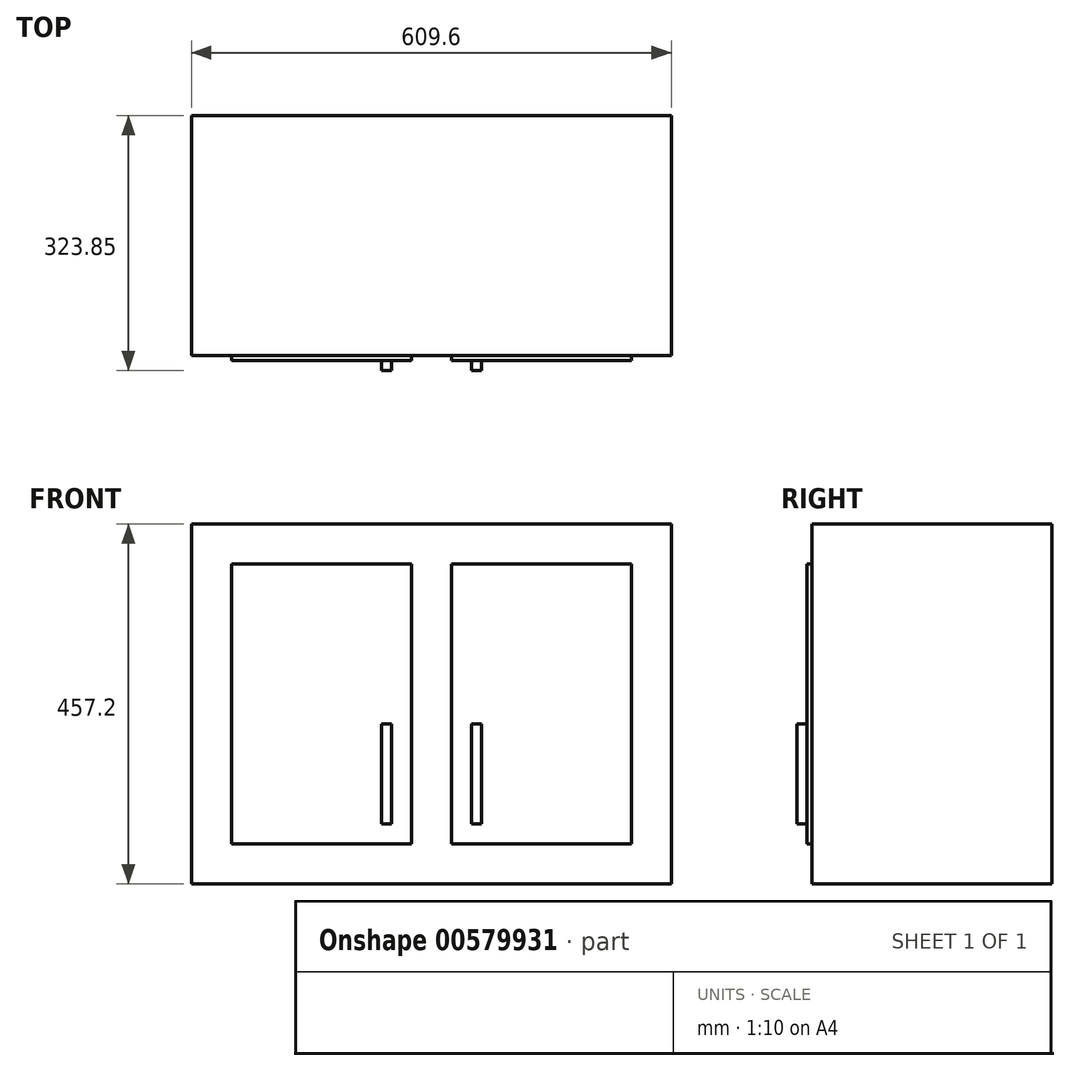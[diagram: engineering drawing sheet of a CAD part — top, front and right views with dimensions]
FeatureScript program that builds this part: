
annotation { "Feature Type Name" : "Feature", "Feature Type Description" : "" }
export const myFeature = defineFeature(function(context is Context, id is Id, definition is map)
    precondition{}
    {
        {
            var Q0;
            Q0=qCreatedBy(makeId("Front.planeOp"),FACE);
            var sketch = newSketch(context, id + "F0", { "sketchPlane" : qUnion([Q0])});
            skLineSegment(sketch, "E0.bottom", {"start": v(-332.33, 262.74) * mm, "end": v(277.27, 262.74) * mm});
            skLineSegment(sketch, "E0.top", {"start": v(-332.33, -194.46) * mm, "end": v(277.27, -194.46) * mm});
            skLineSegment(sketch, "E0.left", {"start": v(-332.33, 262.74) * mm, "end": v(-332.33, -194.46) * mm});
            skLineSegment(sketch, "E0.right", {"start": v(277.27, 262.74) * mm, "end": v(277.27, -194.46) * mm});
            skSolve(sketch);
        }
        {
            var Q0;
            Q0=makeQuery(id+"F0.imprint","IMPRINT",FACE,{"disambiguationData":[TD([[makeQuery(id+"F0.imprint","IMPRINT",EDGE,{"derivedFrom":sQuery(id+"F0.wireOp",EDGE,"E0.bottom")}),-1.0]])]});
            extrude(context, id + "F1", {"entities" : qUnion([Q0]), "depth" : 304.8 * mm, "offsetDistance" : 25.4 * mm});
        }
        {
            var Q0;
            Q0=makeQuery(id+"F1.opExtrude","CAP_FACE",FACE,{"disambiguationData":[OSD([sQuery(id+"F0.wireOp",EDGE,"E0.bottom"),sQuery(id+"F0.wireOp",EDGE,"E0.top"),sQuery(id+"F0.wireOp",EDGE,"E0.left"),sQuery(id+"F0.wireOp",EDGE,"E0.right")])],"isStart":false});
            var sketch = newSketch(context, id + "F2", { "sketchPlane" : qUnion([Q0])});
            skLineSegment(sketch, "E1.bottom", {"start": v(-281.53, 211.94) * mm, "end": v(-52.93, 211.94) * mm});
            skLineSegment(sketch, "E1.top", {"start": v(-281.53, -143.66) * mm, "end": v(-52.93, -143.66) * mm});
            skLineSegment(sketch, "E1.left", {"start": v(-281.53, 211.94) * mm, "end": v(-281.53, -143.66) * mm});
            skLineSegment(sketch, "E1.right", {"start": v(-52.93, 211.94) * mm, "end": v(-52.93, -143.66) * mm});
            skLineSegment(sketch, "E2.bottom", {"start": v(-2.13, 211.94) * mm, "end": v(226.47, 211.94) * mm});
            skLineSegment(sketch, "E2.top", {"start": v(-2.13, -143.66) * mm, "end": v(226.47, -143.66) * mm});
            skLineSegment(sketch, "E2.left", {"start": v(-2.13, 211.94) * mm, "end": v(-2.13, -143.66) * mm});
            skLineSegment(sketch, "E2.right", {"start": v(226.47, 211.94) * mm, "end": v(226.47, -143.66) * mm});
            skSolve(sketch);
        }
        {
            var Q0;
            Q0=makeQuery(id+"F2.imprint","IMPRINT",FACE,{"disambiguationData":[TD([[makeQuery(id+"F2.imprint","IMPRINT",EDGE,{"derivedFrom":sQuery(id+"F2.wireOp",EDGE,"E1.bottom")}),-1.0]])]});
            var Q1;
            Q1=makeQuery(id+"F2.imprint","IMPRINT",FACE,{"disambiguationData":[TD([[makeQuery(id+"F2.imprint","IMPRINT",EDGE,{"derivedFrom":sQuery(id+"F2.wireOp",EDGE,"E2.bottom")}),-1.0]])]});
            extrude(context, id + "F3", {"entities" : qUnion([Q0, Q1]), "operationType" : NewBodyOperationType.ADD, "depth" : 6.35 * mm, "offsetDistance" : 25.4 * mm});
        }
        {
            var Q0;
            Q0=makeQuery(id+"F3.opExtrude","CAP_FACE",FACE,{"disambiguationData":[OSD([sQuery(id+"F2.wireOp",EDGE,"E1.bottom"),sQuery(id+"F2.wireOp",EDGE,"E1.top"),sQuery(id+"F2.wireOp",EDGE,"E1.left"),sQuery(id+"F2.wireOp",EDGE,"E1.right")])],"isStart":false});
            var sketch = newSketch(context, id + "F4", { "sketchPlane" : qUnion([Q0])});
            skLineSegment(sketch, "E3.bottom", {"start": v(-91.03, 8.74) * mm, "end": v(-78.33, 8.74) * mm});
            skLineSegment(sketch, "E3.top", {"start": v(-91.03, -118.26) * mm, "end": v(-78.33, -118.26) * mm});
            skLineSegment(sketch, "E3.left", {"start": v(-91.03, 8.74) * mm, "end": v(-91.03, -118.26) * mm});
            skLineSegment(sketch, "E3.right", {"start": v(-78.33, 8.74) * mm, "end": v(-78.33, -118.26) * mm});
            skLineSegment(sketch, "E4.bottom", {"start": v(23.27, 8.74) * mm, "end": v(35.97, 8.74) * mm});
            skLineSegment(sketch, "E4.top", {"start": v(23.27, -118.26) * mm, "end": v(35.97, -118.26) * mm});
            skLineSegment(sketch, "E4.left", {"start": v(23.27, 8.74) * mm, "end": v(23.27, -118.26) * mm});
            skLineSegment(sketch, "E4.right", {"start": v(35.97, 8.74) * mm, "end": v(35.97, -118.26) * mm});
            skSolve(sketch);
        }
        {
            var Q0;
            Q0 = qSketchRegion(id + "F4", true);
            extrude(context, id + "F5", {"entities" : qUnion([Q0]), "operationType" : NewBodyOperationType.ADD, "depth" : 12.7 * mm, "offsetDistance" : 25.4 * mm});
        }
    });
